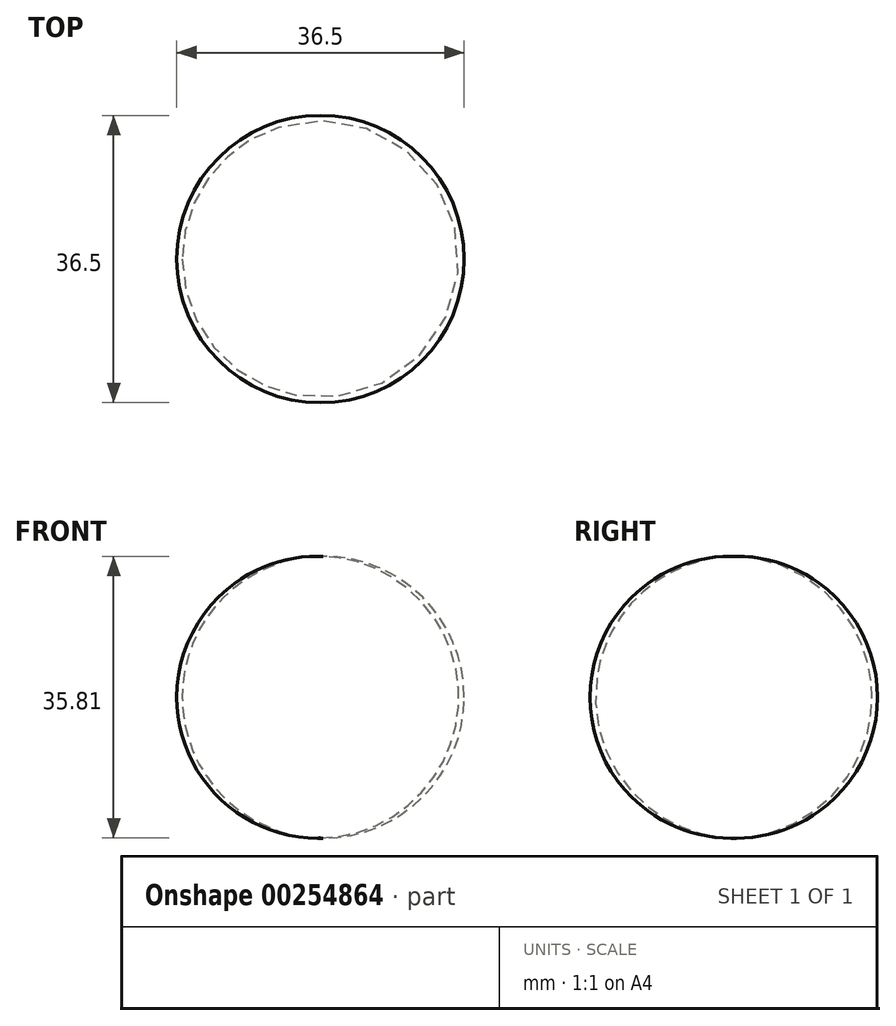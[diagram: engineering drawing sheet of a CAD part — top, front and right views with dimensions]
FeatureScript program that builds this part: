
annotation { "Feature Type Name" : "Feature", "Feature Type Description" : "" }
export const myFeature = defineFeature(function(context is Context, id is Id, definition is map)
    precondition{}
    {
        {
            var Q0;
            Q0=qCreatedBy(makeId("Front.planeOp"),FACE);
            var sketch = newSketch(context, id + "F0", { "sketchPlane" : qUnion([Q0])});
            skLineSegment(sketch, "E0", {"start": v(0, 35.8) * mm, "end": v(0, 0) * mm});
            skArc(sketch, "E1", {"start": v(0, 35.8) * mm, "mid": v(-17.56, 17.9) * mm, "end": v(0, 0) * mm});
            skSolve(sketch);
        }
        {
            var Q0;
            Q0=makeQuery(id+"F0.imprint","IMPRINT",FACE,{"disambiguationData":[TD([[makeQuery(id+"F0.imprint","IMPRINT",EDGE,{"derivedFrom":sQuery(id+"F0.wireOp",EDGE,"E0")}),-1.0]])]});
            var Q1;
            Q1=sQuery(id+"F0.wireOp",EDGE,"E0");
            revolve(context, id + "F1", {"entities" : qUnion([Q0]), "axis" : qUnion([Q1]), "revolveType" : RevolveType.FULL});
        }
    });
